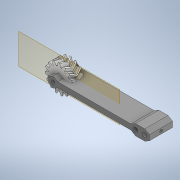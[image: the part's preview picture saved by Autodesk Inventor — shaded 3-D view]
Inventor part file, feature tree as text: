
AUTODESK INVENTOR PART (.ipt)
format: ipt  version: 2020 (Build 240168000, 168)  size: 928,768 bytes
history: native  units: in
note: dims shown in document units (in); Inventor stores cm internally (conversion verified against a paired STEP export)
features: sketch x4, other x3, extrude x3, plane x2, mirror x1, projected_geometry x1
ambient origin geometry x8: Origin, YZ Plane, XZ Plane, XY Plane, X Axis, Y Axis, Z Axis, Center Point
bodies: Solid1 (feature_tree), Solid2 (feature_tree)
feature tree (14):
  other  "Spur Gear1"
  plane  "Work Plane3"
  extrude  "Extrusion1"  Depth=3.4256in
  plane  "Work Plane1"
  extrude  "Extrusion2"  Depth=0.7874in
  sketch  "Sketch4"  dims[d4=0.0in d5=0.0906in]
  extrude  "Extrusion4"  Depth=0.0906in
  mirror  "Mirror3"
  sketch  "Sketch1"  dims[d0=0.1818in d1=3.4256in]
  sketch  "Sketch2"  dims[d2=0.122in d3=0.7874in]
  sketch  "Sketch5"  dims[d6=0.7874in d7=0.0in d29=0.315in d31=0.315in d33=0.1476in d34=0.2362in d35=0.0in d38=0.315in d69=2.4807in d70=0.3937in d71=0.1969in]
  other  "Solid1::Spur Gear1"
  other  "TaggingFeature1"
  projected_geometry  "Projected Loop11"
